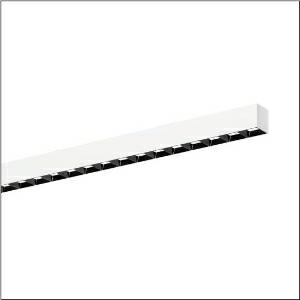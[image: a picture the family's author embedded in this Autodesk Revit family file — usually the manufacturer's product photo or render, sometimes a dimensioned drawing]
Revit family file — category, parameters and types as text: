
# Revit family: silica_21_51mx24da44wb
name_source: partatom
category: Lighting Fixtures
units: mm (PartAtom-declared; Revit-internal decimal feet)

## family parameters
Cut with Voids When Loaded = No
Host = Face
Light Source = No
Part Type = Normal
Room Calculation Point = No
Round Connector Dimension = Use Diameter
Shared = No

## types (1)
- --- (1 x LED, 4320 lm, 30 W, 4000K)
    Apparent Load = 30 VA
    CIE Flux Codes = 74 94 99 100 100
    Color Rendering = 80
    Color Temperature = 4000K
    Default Elevation = 1800 mm
    Description = Silica 21, office luminaire, primary light control with darklight reflector, of PMMA, black, CAT 2 (L<= 3000cd/m²), light emission: direct distribution, primary light characteristic: asymmetric, installation type: surface-mounted, LED, rated luminous flux: 4.320lm, luminous efficacy: 144lm/W, light colour: 840, colour temperature: 4000K, control gear: DALI 2, with terminal, 3+2-pole, max. 2.5mm², mains connection: 220..240V, AC, 50/60Hz, rated input power: 30W, luminaire housing, of aluminium, traffic white (RAL 9016), length: 1.204mm, width: 53mm, height: 53mm, protection rating (complete): IP20, insulation class (complete): insulation class I (protective earthing), certification: CE, permissible operating ambient temperature: 0..+35°C, standard: EN 50419, packaging unit: 1 piece
    Height = 53 mm
    Lamp = 1 x LED
    Lamp Light Flux = 4320 lm
    Lamp Power = 30 W
    Lamp count = 1
    Length = 1204 mm
    Luminous efficacy = 144 lm/W
    Manufacturer = Siteco
    ModVariant = No
    Model = 51MX24DA44WB
    Mounting Place = Ceiling
    Mounting Type = Surface mounted
    Number of Poles = 1
    OnlyDefault = Yes
    Power Factor = 1
    Product Name = Silica 21
    Product group = office luminaire | ceiling mounted
    ProductGroupID = 301
    Protection Class = Protection class I
    Protection Degree = IP 20
    RLX_Detail_Level = 1
    RLX_Emergency_Light_Flux = 0 lm
    RLX_Emergency_Type = 0
    RLX_Emergency_Type_DB = No
    RlxData = <blob elided: 41521 chars, md5=3fd8a6fc>
    Socket = socket
    Standby Power = 0 W
    System Light Flux = 4320 lm
    System Power = 30 W
    Type Comments = factory setting: luminous flux: 100 % | dim-lin: 254 | 418 mA
    Type Image = l_1335873.jpg
    URL = http://relux.com
    VarID = @adj_123453
    Voltage = 0 V
    Weight = 0.00 kg
    Width = 53 mm

## geometry (parser evidence)
native form markers: Blend x4, Sweep x11
no freeform markers — native parametric forms only
